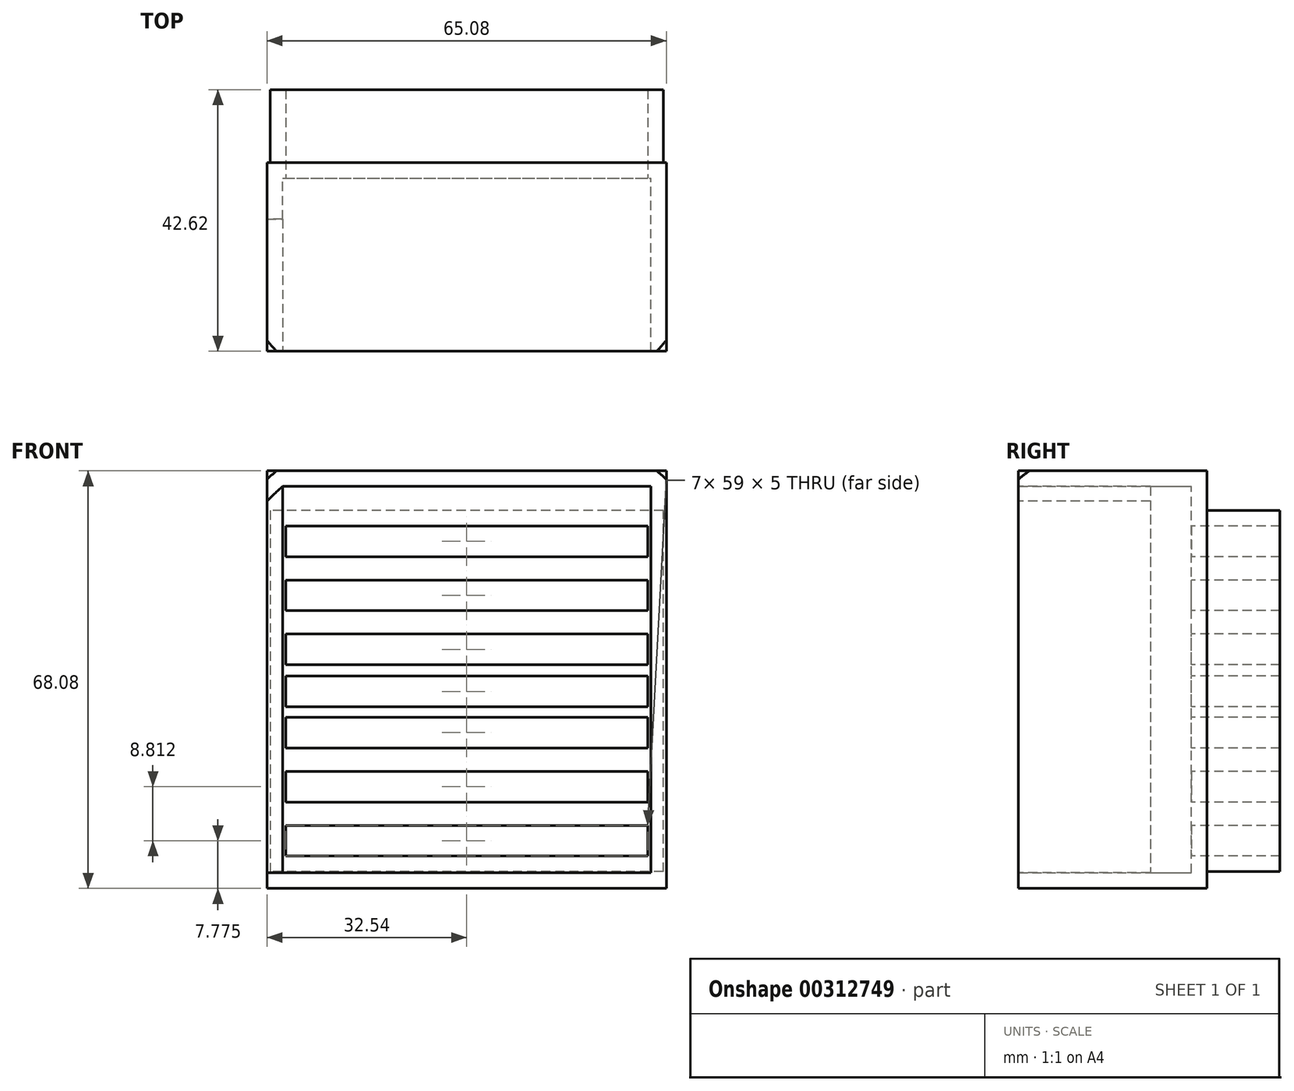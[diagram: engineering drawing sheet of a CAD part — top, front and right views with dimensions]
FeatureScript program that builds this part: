
annotation { "Feature Type Name" : "Feature", "Feature Type Description" : "" }
export const myFeature = defineFeature(function(context is Context, id is Id, definition is map)
    precondition{}
    {
        {
            var Q0;
            Q0=qCreatedBy(makeId("Front.planeOp"),FACE);
            var sketch = newSketch(context, id + "F0", { "sketchPlane" : qUnion([Q0])});
            skLineSegment(sketch, "E0", {"start": v(-56, 0) * mm, "end": v(56, 0) * mm});
            skArc(sketch, "E1", {"start": v(56, 0) * mm, "mid": v(0, 55) * mm, "end": v(-56, 0) * mm});
            skSolve(sketch);
        }
        {
            var Q0;
            Q0 = qSketchRegion(id + "F0", true);
            var Q1;
            Q1=sQuery(id+"F0.wireOp",EDGE,"E0");
            revolve(context, id + "F1", {"entities" : qUnion([Q0]), "axis" : qUnion([Q1]), "revolveType" : RevolveType.FULL});
        }
        {
            var Q0;
            Q0=qCreatedBy(makeId("Front.planeOp"),FACE);
            var sketch = newSketch(context, id + "F2", { "sketchPlane" : qUnion([Q0])});
            skLineSegment(sketch, "E2", {"start": v(0, 33.36) * mm, "end": v(-30, 33.36) * mm});
            skLineSegment(sketch, "E3", {"start": v(-30, 33.36) * mm, "end": v(30, 33.36) * mm});
            skLineSegment(sketch, "E4", {"start": v(-30, 33.36) * mm, "end": v(-30, -29.64) * mm});
            skLineSegment(sketch, "E5", {"start": v(-30, -29.64) * mm, "end": v(30, -29.64) * mm});
            skLineSegment(sketch, "E6", {"start": v(30, -29.64) * mm, "end": v(30, 33.36) * mm});
            skSolve(sketch);
        }
        {
            var Q0;
            Q0 = qSketchRegion(id + "F2", true);
            extrude(context, id + "F3", {"entities" : qUnion([Q0]), "operationType" : NewBodyOperationType.REMOVE, "depth" : 130.3 * mm});
        }
        {
            var Q0;
            Q0=qCreatedBy(makeId("Right.planeOp"),FACE);
            var sketch = newSketch(context, id + "F4", { "sketchPlane" : qUnion([Q0])});
            skLineSegment(sketch, "E7", {"start": v(-32.1, 33.36) * mm, "end": v(-32.1, -29.65) * mm});
            skLineSegment(sketch, "E8", {"start": v(-32.1, -29.65) * mm, "end": v(-54.45, -29.65) * mm});
            skLineSegment(sketch, "E9", {"start": v(-54.45, -29.65) * mm, "end": v(-54.45, 33.36) * mm});
            skLineSegment(sketch, "E10", {"start": v(-54.45, 33.36) * mm, "end": v(-32.1, 33.36) * mm});
            skSolve(sketch);
        }
        {
            var Q0;
            Q0 = qSketchRegion(id + "F4", true);
            extrude(context, id + "F5", {"entities" : qUnion([Q0]), "operationType" : NewBodyOperationType.REMOVE, "endBound" : BoundingType.SYMMETRIC, "oppositeDirection" : true, "depth" : 124.97 * mm});
        }
        {
            var Q0;
            Q0=makeQuery(id+"F3.boolean.opBoolean","COPY",FACE,{"derivedFrom":makeQuery(id+"F3.opExtrude","CAP_FACE",FACE,{"disambiguationData":[OSD([sQuery(id+"F2.wireOp",EDGE,"E3"),sQuery(id+"F2.wireOp",EDGE,"E4"),sQuery(id+"F2.wireOp",EDGE,"E5"),sQuery(id+"F2.wireOp",EDGE,"E6")])],"isStart":true})});
            var sketch = newSketch(context, id + "F6", { "sketchPlane" : qUnion([Q0])});
            skLineSegment(sketch, "E11", {"start": v(-29.5, 26.9) * mm, "end": v(-29.5, 21.9) * mm});
            skLineSegment(sketch, "E12", {"start": v(-29.5, 21.9) * mm, "end": v(29.5, 21.9) * mm});
            skLineSegment(sketch, "E13", {"start": v(29.5, 21.9) * mm, "end": v(29.5, 26.9) * mm});
            skLineSegment(sketch, "E14", {"start": v(29.5, 26.9) * mm, "end": v(-29.5, 26.9) * mm});
            skLineSegment(sketch, "E15.MirrorCS", {"start": v(-29.5, -21.9) * mm, "end": v(29.5, -21.9) * mm});
            skLineSegment(sketch, "E16.MirrorCS", {"start": v(29.5, -26.9) * mm, "end": v(-29.5, -26.9) * mm});
            skLineSegment(sketch, "E17.MirrorCS", {"start": v(29.5, -21.9) * mm, "end": v(29.5, -26.9) * mm});
            skLineSegment(sketch, "E18.MirrorCS", {"start": v(-29.5, -26.9) * mm, "end": v(-29.5, -21.9) * mm});
            skLineSegment(sketch, "E19", {"start": v(-29.5, 18.1) * mm, "end": v(29.5, 18.1) * mm});
            skLineSegment(sketch, "E20", {"start": v(29.5, 18.1) * mm, "end": v(29.5, 13.1) * mm});
            skLineSegment(sketch, "E21", {"start": v(29.5, 13.1) * mm, "end": v(-29.5, 13.1) * mm});
            skLineSegment(sketch, "E22", {"start": v(-29.5, 13.1) * mm, "end": v(-29.5, 18.1) * mm});
            skLineSegment(sketch, "E23", {"start": v(-29.5, 9.28) * mm, "end": v(29.5, 9.28) * mm});
            skLineSegment(sketch, "E24", {"start": v(29.5, 9.28) * mm, "end": v(29.5, 4.28) * mm});
            skLineSegment(sketch, "E25", {"start": v(29.5, 4.28) * mm, "end": v(-29.5, 4.28) * mm});
            skLineSegment(sketch, "E26", {"start": v(-29.5, 4.28) * mm, "end": v(-29.5, 9.28) * mm});
            skLineSegment(sketch, "E27.MirrorCS", {"start": v(29.5, -4.28) * mm, "end": v(-29.5, -4.28) * mm});
            skLineSegment(sketch, "E28.MirrorCS", {"start": v(-29.5, -9.28) * mm, "end": v(29.5, -9.28) * mm});
            skLineSegment(sketch, "E29.MirrorCS", {"start": v(29.5, -13.1) * mm, "end": v(-29.5, -13.1) * mm});
            skLineSegment(sketch, "E30.MirrorCS", {"start": v(-29.5, -18.1) * mm, "end": v(29.5, -18.1) * mm});
            skLineSegment(sketch, "E31.MirrorCS", {"start": v(-29.5, -13.1) * mm, "end": v(-29.5, -18.1) * mm});
            skLineSegment(sketch, "E32.MirrorCS", {"start": v(29.5, -18.1) * mm, "end": v(29.5, -13.1) * mm});
            skLineSegment(sketch, "E33.MirrorCS", {"start": v(29.5, -9.28) * mm, "end": v(29.5, -4.28) * mm});
            skLineSegment(sketch, "E34.MirrorCS", {"start": v(-29.5, -4.28) * mm, "end": v(-29.5, -9.28) * mm});
            skLineSegment(sketch, "E35", {"start": v(-29.5, 2.43) * mm, "end": v(29.5, 2.43) * mm});
            skLineSegment(sketch, "E36", {"start": v(29.5, 2.43) * mm, "end": v(29.5, -2.57) * mm});
            skLineSegment(sketch, "E37", {"start": v(29.5, -2.57) * mm, "end": v(-29.5, -2.57) * mm});
            skLineSegment(sketch, "E38", {"start": v(-29.5, -2.57) * mm, "end": v(-29.5, 2.43) * mm});
            skSolve(sketch);
        }
        {
            var Q0;
            Q0 = qSketchRegion(id + "F6", true);
            extrude(context, id + "F7", {"entities" : qUnion([Q0]), "operationType" : NewBodyOperationType.REMOVE, "oppositeDirection" : true, "depth" : 35.81 * mm});
        }
        {
            var Q0;
            Q0=makeQuery(id+"F1.opRevolve","SWEPT_FACE",FACE,{"disambiguationData":[OSD([sQuery(id+"F0.wireOp",EDGE,"E1")])]});
            var Q1;
            Q1=makeQuery(id+"F1.opRevolve","SWEPT_BODY",BODY,{"disambiguationData":[OSD([sQuery(id+"F0.wireOp",EDGE,"E0"),sQuery(id+"F0.wireOp",EDGE,"E1")])]});
            shell(context, id + "F8", {"entities" : qUnion([Q0]), "parts" : qUnion([Q1]), "thickness" : 2.54 * mm});
        }
        {
            var Q0;
            Q0=qCreatedBy(makeId("Right.planeOp"),FACE);
            var sketch = newSketch(context, id + "F9", { "sketchPlane" : qUnion([Q0])});
            skLineSegment(sketch, "E39", {"start": v(14.42, 0) * mm, "end": v(14.42, 32.5) * mm});
            skLineSegment(sketch, "E40", {"start": v(14.42, 32.5) * mm, "end": v(14.42, -34.28) * mm});
            skLineSegment(sketch, "E41", {"start": v(14.42, -34.28) * mm, "end": v(50.03, -34.28) * mm});
            skLineSegment(sketch, "E42", {"start": v(50.03, -34.28) * mm, "end": v(50.03, 32.5) * mm});
            skLineSegment(sketch, "E43", {"start": v(50.03, 32.5) * mm, "end": v(14.42, 32.5) * mm});
            skSolve(sketch);
        }
        {
            var Q0;
            Q0 = qSketchRegion(id + "F9", true);
            extrude(context, id + "F10", {"entities" : qUnion([Q0]), "operationType" : NewBodyOperationType.REMOVE, "endBound" : BoundingType.SYMMETRIC, "oppositeDirection" : true, "depth" : 89.92 * mm});
        }
        {
            var Q0;
            Q0=makeQuery(id+"F5.boolean.opBoolean","COPY",FACE,{"disambiguationData":[TD([makeQuery(id+"F3.boolean.opBoolean","COPY",FACE,{"derivedFrom":makeQuery(id+"F3.opExtrude","SWEPT_FACE",FACE,{"disambiguationData":[OSD([sQuery(id+"F2.wireOp",EDGE,"E6")])]})})])],"derivedFrom":makeQuery(id+"F5.opExtrude","SWEPT_FACE",FACE,{"disambiguationData":[OSD([sQuery(id+"F4.wireOp",EDGE,"E7")])]})});
            var sketch = newSketch(context, id + "F11", { "sketchPlane" : qUnion([Q0])});
            skFitSpline(sketch, "E44.0", {"points": [v(30.56, -32.85) * mm, v(31.8, -31.72) * mm, v(33.56, -29.94) * mm, v(35.68, -27.39) * mm, v(37.16, -25.39) * mm, v(38.53, -23.3) * mm, v(39.59, -21.5) * mm, v(40.37, -20) * mm, v(41.1, -18.5) * mm, v(42.28, -15.84) * mm, v(43.36, -12.7) * mm, v(44.17, -9.48) * mm, v(44.56, -7.43) * mm, v(44.8, -5.77) * mm, v(45, -4.1) * mm, v(45.22, -1.2) * mm, v(45.18, 2.11) * mm, v(44.87, 5.42) * mm, v(44.55, 7.5) * mm, v(44.22, 9.14) * mm, v(43.85, 10.77) * mm, v(43.08, 13.58) * mm, v(41.94, 16.7) * mm, v(40.71, 19.34) * mm, v(39.95, 20.82) * mm, v(39.34, 21.92) * mm, v(38.7, 23) * mm, v(37.8, 24.42) * mm, v(36.15, 26.82) * mm, v(34.05, 29.39) * mm, v(31.74, 31.78) * mm, v(29.9, 33.48) * mm, v(27.94, 35.09) * mm, v(26.6, 36.08) * mm, v(25.9, 36.56) * mm]});
            skLineSegment(sketch, "E44.2", {"start": v(30, -29.65) * mm, "end": v(30, 33.36) * mm});
            skFitSpline(sketch, "E44.3", {"points": [v(-33.75, -29.65) * mm, v(-32.5, -29.65) * mm, v(-31.25, -29.65) * mm, v(-30, -29.65) * mm]});
            skLineSegment(sketch, "E44.4", {"start": v(-30, 33.36) * mm, "end": v(-30, -29.64) * mm});
            skFitSpline(sketch, "E44.5", {"points": [v(-25.9, 36.56) * mm, v(-27.28, 35.6) * mm, v(-29.91, 33.55) * mm, v(-32.87, 30.67) * mm, v(-35.05, 28.17) * mm, v(-36.32, 26.53) * mm, v(-37.3, 25.17) * mm, v(-38.23, 23.77) * mm, v(-39.32, 21.98) * mm, v(-40.5, 19.79) * mm, v(-41.56, 17.53) * mm, v(-42.48, 15.22) * mm, v(-43.15, 13.25) * mm, v(-43.61, 11.64) * mm, v(-44.04, 10.01) * mm, v(-44.47, 7.96) * mm, v(-44.86, 5.5) * mm, v(-45.18, 2.2) * mm, v(-45.22, -0.71) * mm, v(-45.07, -3.22) * mm, v(-44.92, -4.9) * mm, v(-44.65, -6.97) * mm, v(-44.18, -9.42) * mm, v(-43.58, -11.84) * mm, v(-42.84, -14.22) * mm, v(-42.11, -16.17) * mm, v(-41.46, -17.71) * mm, v(-40.76, -19.24) * mm, v(-39.81, -21.1) * mm, v(-38.56, -23.27) * mm, v(-36.73, -26.04) * mm, v(-34.17, -29.31) * mm, v(-31.8, -31.72) * mm, v(-30.56, -32.85) * mm]});
            skLineSegment(sketch, "E45", {"start": v(30, -29.64) * mm, "end": v(33.75, -29.65) * mm});
            skSolve(sketch);
        }
        {
            var Q0;
            Q0 = qSketchRegion(id + "F11", true);
            var Q1;
            Q1=makeQuery(id+"F5.boolean.opBoolean","COPY",FACE,{"disambiguationData":[TD([makeQuery(id+"F3.boolean.opBoolean","COPY",FACE,{"derivedFrom":makeQuery(id+"F3.opExtrude","SWEPT_FACE",FACE,{"disambiguationData":[OSD([sQuery(id+"F2.wireOp",EDGE,"E4")])]})})])],"derivedFrom":makeQuery(id+"F5.opExtrude","SWEPT_FACE",FACE,{"disambiguationData":[OSD([sQuery(id+"F4.wireOp",EDGE,"E7")])]})});
            extrude(context, id + "F12", {"entities" : qUnion([Q0, Q1]), "operationType" : NewBodyOperationType.REMOVE, "oppositeDirection" : true, "depth" : 25.4 * mm});
        }
        {
            var Q0;
            Q0=qCreatedBy(makeId("Front.planeOp"),FACE);
            var sketch = newSketch(context, id + "F13", { "sketchPlane" : qUnion([Q0])});
            skLineSegment(sketch, "E46.bottom", {"start": v(-33.96, 35.98) * mm, "end": v(-54.4, 35.98) * mm});
            skLineSegment(sketch, "E46.top", {"start": v(-33.96, -31.95) * mm, "end": v(-54.4, -31.95) * mm});
            skLineSegment(sketch, "E46.left", {"start": v(-33.96, 35.98) * mm, "end": v(-33.96, -31.95) * mm});
            skLineSegment(sketch, "E46.right", {"start": v(-54.4, 35.98) * mm, "end": v(-54.4, -31.95) * mm});
            skLineSegment(sketch, "E47.bottom", {"start": v(34.54, 35.98) * mm, "end": v(48.35, 35.98) * mm});
            skLineSegment(sketch, "E47.top", {"start": v(34.54, -42.02) * mm, "end": v(48.35, -42.02) * mm});
            skLineSegment(sketch, "E47.left", {"start": v(34.54, 35.98) * mm, "end": v(34.54, -42.02) * mm});
            skLineSegment(sketch, "E47.right", {"start": v(48.35, 35.98) * mm, "end": v(48.35, -42.02) * mm});
            skSolve(sketch);
        }
        {
            var Q0;
            Q0 = qSketchRegion(id + "F13", true);
            extrude(context, id + "F14", {"entities" : qUnion([Q0]), "operationType" : NewBodyOperationType.REMOVE, "endBound" : BoundingType.THROUGH_ALL, "depth" : 25.4 * mm});
        }
        {
            var Q0;
            Q0=qCreatedBy(makeId("Top.planeOp"),FACE);
            var sketch = newSketch(context, id + "F15", { "sketchPlane" : qUnion([Q0])});
            skLineSegment(sketch, "E48.bottom", {"start": v(-37.7, -28.2) * mm, "end": v(42.02, -28.2) * mm});
            skLineSegment(sketch, "E48.top", {"start": v(-37.7, -46.62) * mm, "end": v(42.02, -46.62) * mm});
            skLineSegment(sketch, "E48.left", {"start": v(-37.7, -28.2) * mm, "end": v(-37.7, -46.62) * mm});
            skLineSegment(sketch, "E48.right", {"start": v(42.02, -28.2) * mm, "end": v(42.02, -46.62) * mm});
            skSolve(sketch);
        }
        {
            var Q0;
            Q0 = qSketchRegion(id + "F15", true);
            extrude(context, id + "F16", {"entities" : qUnion([Q0]), "operationType" : NewBodyOperationType.REMOVE, "endBound" : BoundingType.SYMMETRIC, "oppositeDirection" : true, "depth" : 117.35 * mm});
        }
    });
